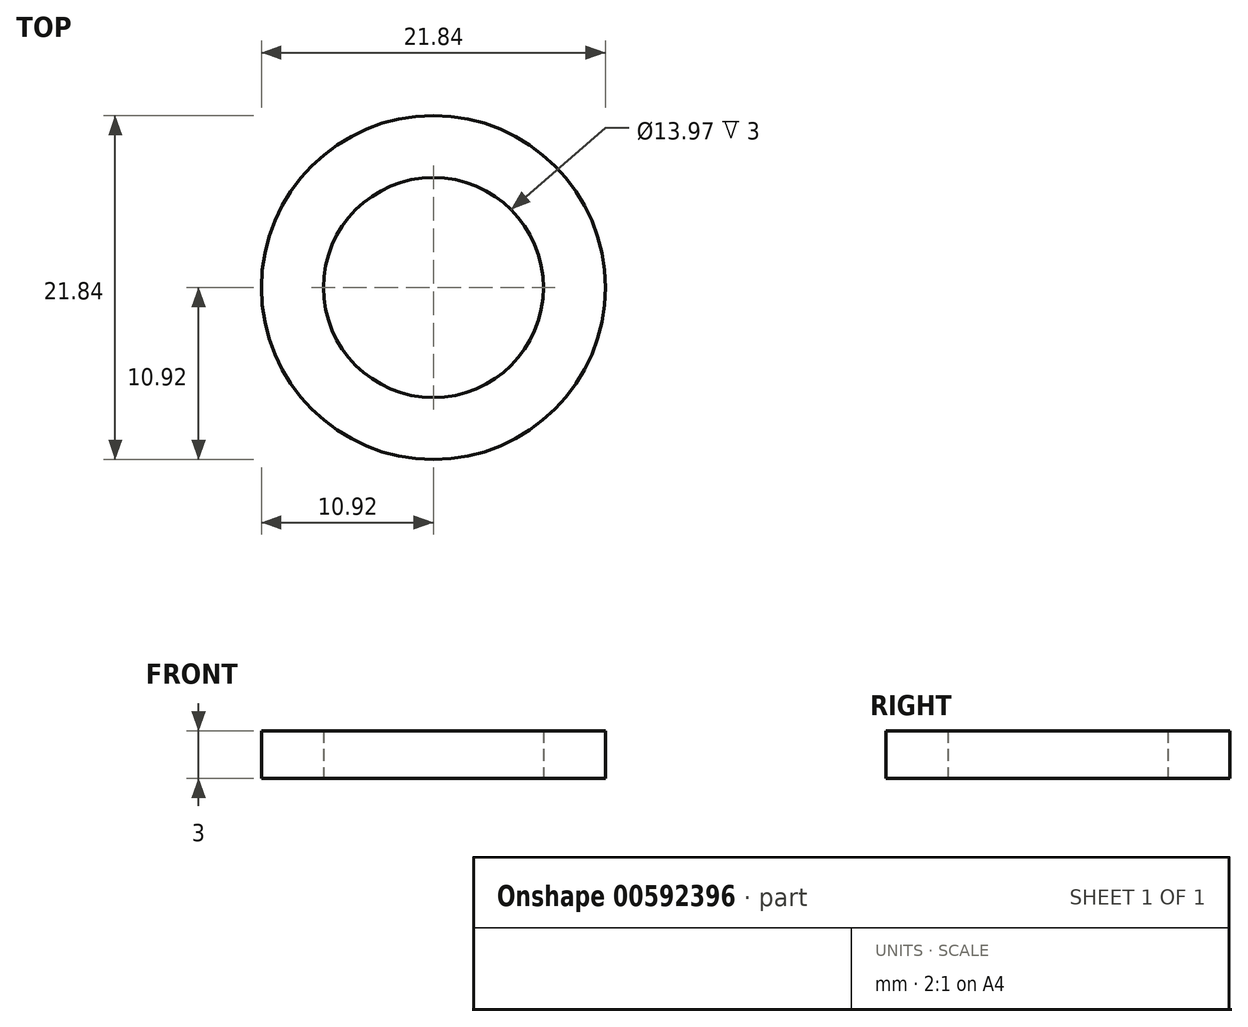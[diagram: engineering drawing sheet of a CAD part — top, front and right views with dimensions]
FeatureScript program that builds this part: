
annotation { "Feature Type Name" : "Feature", "Feature Type Description" : "" }
export const myFeature = defineFeature(function(context is Context, id is Id, definition is map)
    precondition{}
    {
        {
            var Q0;
            Q0=qCreatedBy(makeId("Top.planeOp"),FACE);
            var sketch = newSketch(context, id + "F0", { "sketchPlane" : qUnion([Q0])});
            skCircle(sketch, "E0", {"center": v(0, 0) * mm, "radius": 6.99 * mm});
            skCircle(sketch, "E1", {"center": v(0, 0) * mm, "radius": 10.92 * mm});
            skSolve(sketch);
        }
        {
            var Q0;
            Q0=makeQuery(id+"F0.imprint","IMPRINT",FACE,{"disambiguationData":[TD([[makeQuery(id+"F0.imprint","IMPRINT",EDGE,{"derivedFrom":sQuery(id+"F0.wireOp",EDGE,"E0")}),-1.0]])]});
            extrude(context, id + "F1", {"entities" : qUnion([Q0]), "depth" : 3 * mm, "offsetDistance" : 25 * mm});
        }
    });
